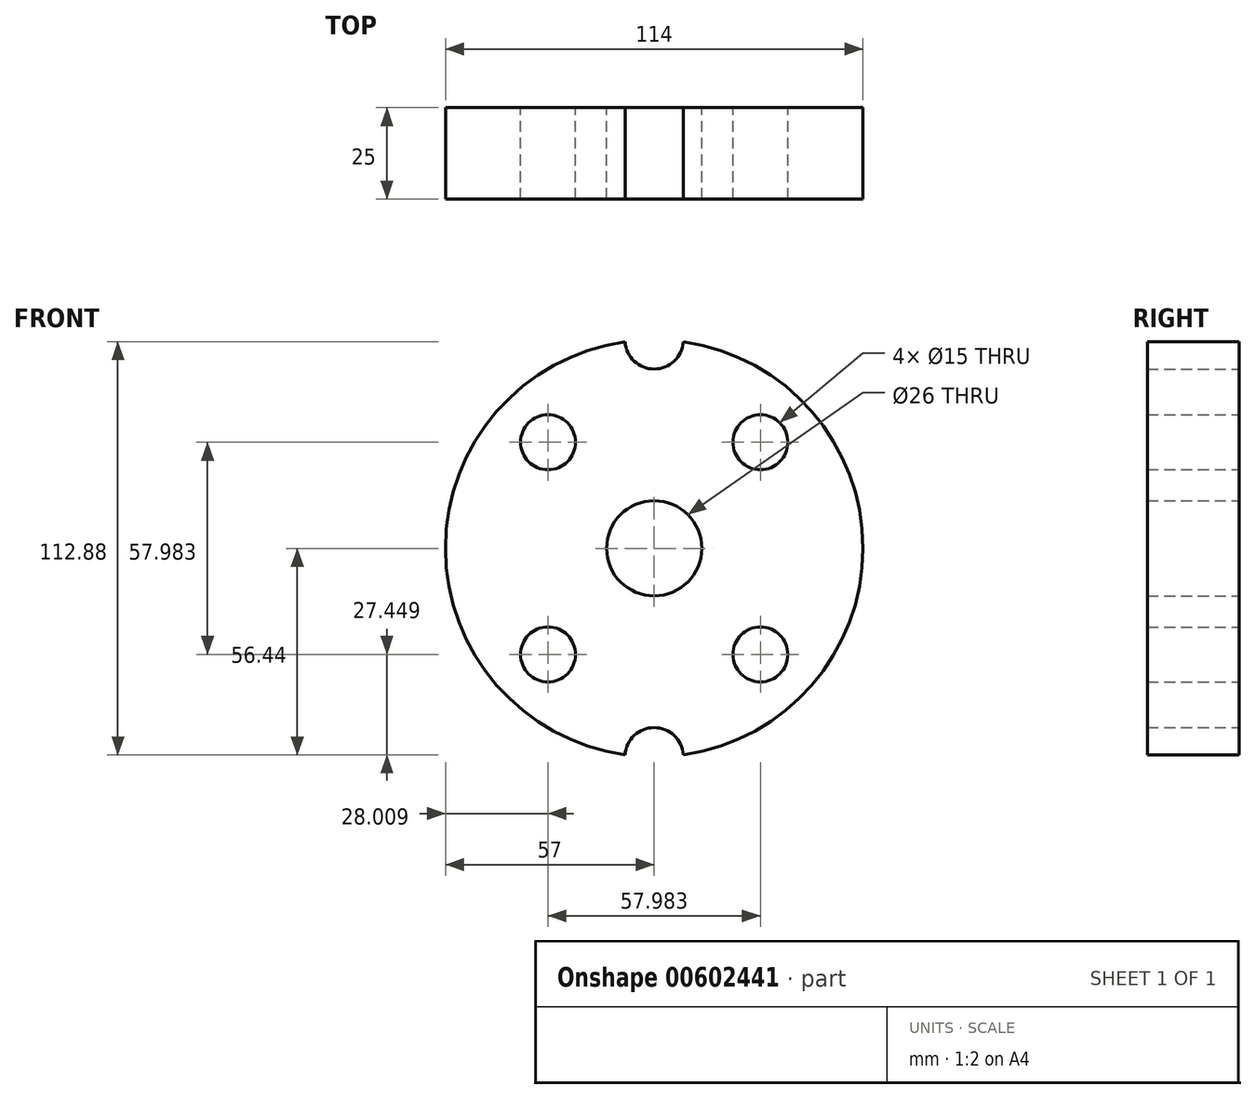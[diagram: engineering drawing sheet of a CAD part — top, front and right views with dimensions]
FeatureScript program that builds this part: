
annotation { "Feature Type Name" : "Feature", "Feature Type Description" : "" }
export const myFeature = defineFeature(function(context is Context, id is Id, definition is map)
    precondition{}
    {
        {
            var Q0;
            Q0=qCreatedBy(makeId("Front.planeOp"),FACE);
            var sketch = newSketch(context, id + "F0", { "sketchPlane" : qUnion([Q0])});
            skArc(sketch, "E0", {"start": v(-7.98, 56.44) * mm, "mid": v(-57, 0) * mm, "end": v(-7.98, -56.44) * mm});
            skCircle(sketch, "E1", {"center": v(0, 0) * mm, "radius": 13 * mm});
            skCircle(sketch, "E2", {"center": v(0, 0) * mm, "radius": 25 * mm});
            skPoint(sketch, "E3", {"position": v(-41, 0) * mm});
            skCircle(sketch, "E4", {"center": v(-29, 29) * mm, "radius": 7.5 * mm});
            skCircle(sketch, "E5", {"center": v(-29, -29) * mm, "radius": 7.5 * mm});
            skCircle(sketch, "E6", {"center": v(29, -29) * mm, "radius": 7.5 * mm});
            skCircle(sketch, "E7", {"center": v(29, 29) * mm, "radius": 7.5 * mm});
            skArc(sketch, "E8", {"start": v(-7.98, 56.44) * mm, "mid": v(0, 49) * mm, "end": v(7.98, 56.44) * mm});
            skArc(sketch, "E9", {"start": v(7.98, -56.44) * mm, "mid": v(0, -49) * mm, "end": v(-7.98, -56.44) * mm});
            skArc(sketch, "E10.trimOffspring", {"start": v(7.98, -56.44) * mm, "mid": v(57, 0) * mm, "end": v(7.98, 56.44) * mm});
            skSolve(sketch);
        }
        {
            var Q0;
            Q0 = qSketchRegion(id + "F0", true);
            var Q1;
            Q1=makeQuery(id+"F0.imprint","IMPRINT",FACE,{"disambiguationData":[TD([[makeQuery(id+"F0.imprint","IMPRINT",EDGE,{"derivedFrom":sQuery(id+"F0.wireOp",EDGE,"E1")}),-1.0]])]});
            extrude(context, id + "F1", {"entities" : qUnion([Q0, Q1]), "depth" : 25 * mm, "offsetDistance" : 25 * mm});
        }
    });
